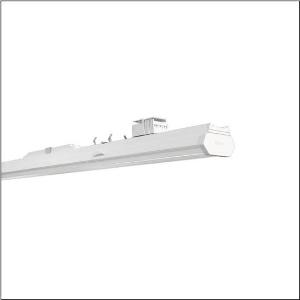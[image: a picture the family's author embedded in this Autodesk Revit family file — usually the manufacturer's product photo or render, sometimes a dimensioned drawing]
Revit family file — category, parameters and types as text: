
# Revit family: licross_r__21_protected_ho_52tp13cn4c5s_cd4a
name_source: partatom
category: Lighting Fixtures
units: mm (PartAtom-declared; Revit-internal decimal feet)

## family parameters
Cut with Voids When Loaded = No
Host = Face
Light Source = No
Part Type = Normal
Room Calculation Point = No
Round Connector Dimension = Use Diameter
Shared = No

## types (1)
- --- (1 x LED, 12680 lm, 68.9 W, 4000K)
    Apparent Load = 69 VA
    CIE Flux Codes = 89 96 99 100 99
    Color Rendering = 80
    Color Temperature = 4000K
    Default Elevation = 1800 mm
    Description = Licross® 21 Protected HO, luminaire insert, of sheet steel, galvanised, coil coated, white, length: 1.500mm, width: 66mm, height: 67mm, LED rated luminous flux: 12.690lm, light colour: 840, SDCM (Standard Deviation of Colour Matching)MacAdam ≤ 3 SDCM (initial), control gear: ON/OFF Multilumen, CLOi, with plug, 3-pole, with phase selection, mains connection: 220..240V, AC, 50/60Hz, start of lifetime: 69W, end of service life: 83W, internal wiring halogen-free, primary light control with lens, of plastic, primary optical cover: cover, of PMMA, light emission: direct distribution, primary light characteristic: symmetric, protection rating (complete): IP64, insulation class (complete): insulation class I (protective earthing), certification: CE, ENEC, VDE, UKCA, protection symbol: D if used in an environment with conductive dust loads with corresponding accessories, impact resistance: IK06, permissible ambient temperature for indoor applications: -35..+35°C, corresponds to IFS (International Featured Standards) requirements for safety and quality in the food industry, reducing of maximum allowable ambient temperature of 5°C with ceiling mounting, LABS conformity tested according to VDMA 24364:2018-05, packaging unit: 1 piece
    Height = 92 mm
    Lamp = 1 x LED
    Lamp Light Flux = 12680 lm
    Lamp Power = 68.9 W
    Lamp count = 1
    Length = 1500 mm
    Luminous efficacy = 184 lm/W
    Manufacturer = Siteco
    ModVariant = No
    Model = 52TP13CN4C5S
    Mounting Place = Ceiling
    Mounting Type = Pendant
    Number of Poles = 1
    OnlyDefault = Yes
    Power Factor = 1
    Product Name = Licross® 21 Protected HO
    Product group = luminaire insert | ceiling pendant
    ProductGroupID = 901
    Protection Class = Protection class I
    Protection Degree = IP 64
    RLX_Detail_Level = 1
    RLX_Emergency_Light_Flux = 0 lm
    RLX_Emergency_Type = 0
    RLX_Emergency_Type_DB = No
    RlxData = <blob elided: 22153 chars, md5=2f7e35b8>
    Socket = socket
    Standby Power = 0 W
    System Light Flux = 12680 lm
    System Power = 69 W
    Type Comments = factory setting: luminous flux: 100 % | (A | C | E) | 162 mA
    Type Image = l_1256148.jpg
    URL = http://relux.com
    VarID = @adj_114735
    Voltage = 0 V
    Weight = 0.00 kg
    Width = 88 mm

## geometry (parser evidence)
native form markers: Blend x4, Sweep x11
no freeform markers — native parametric forms only
